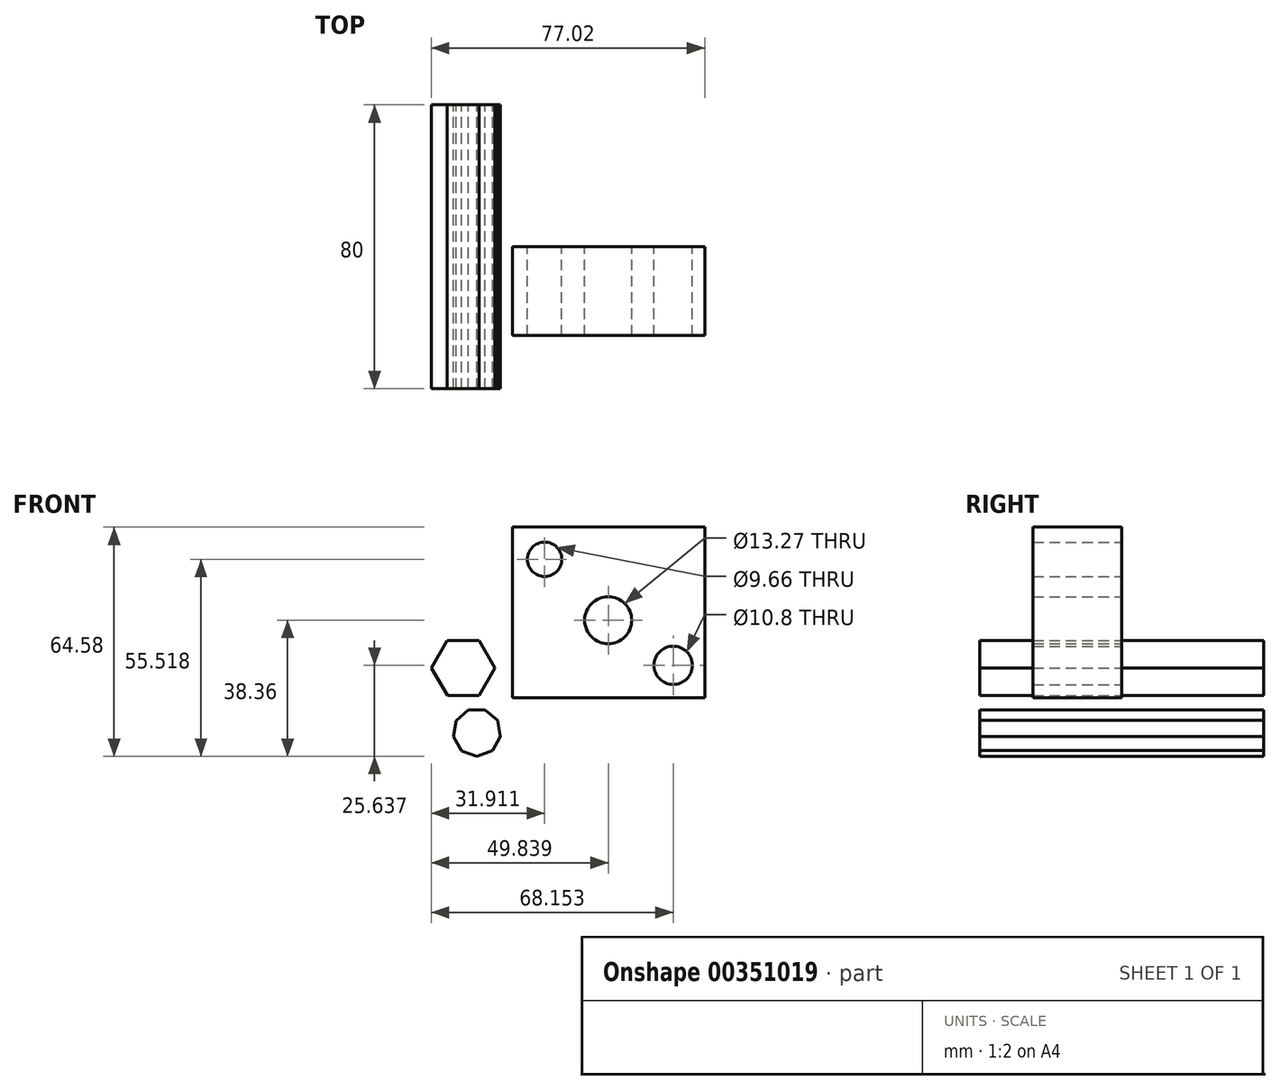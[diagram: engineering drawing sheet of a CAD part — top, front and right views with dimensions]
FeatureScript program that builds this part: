
annotation { "Feature Type Name" : "Feature", "Feature Type Description" : "" }
export const myFeature = defineFeature(function(context is Context, id is Id, definition is map)
    precondition{}
    {
        {
            var Q0;
            Q0=qCreatedBy(makeId("Front.planeOp"),FACE);
            var sketch = newSketch(context, id + "F0", { "sketchPlane" : qUnion([Q0])});
            skLineSegment(sketch, "E0.bottom", {"start": v(0, 0) * mm, "end": v(54.17, 0) * mm});
            skLineSegment(sketch, "E0.top", {"start": v(0, 48.1) * mm, "end": v(54.17, 48.1) * mm});
            skLineSegment(sketch, "E0.left", {"start": v(0, 0) * mm, "end": v(0, 48.1) * mm});
            skLineSegment(sketch, "E0.right", {"start": v(54.17, 0) * mm, "end": v(54.17, 48.1) * mm});
            skCircle(sketch, "E1", {"center": v(9.06, 39.04) * mm, "radius": 4.83 * mm});
            skCircle(sketch, "E2", {"center": v(26.99, 21.88) * mm, "radius": 6.63 * mm});
            skCircle(sketch, "E3", {"center": v(45.3, 9.16) * mm, "radius": 5.4 * mm});
            skSolve(sketch);
        }
        {
            var Q0;
            Q0=makeQuery(id+"F0.imprint","IMPRINT",FACE,{"disambiguationData":[TD([[makeQuery(id+"F0.imprint","IMPRINT",EDGE,{"derivedFrom":sQuery(id+"F0.wireOp",EDGE,"E0.bottom")}),1.0]])]});
            extrude(context, id + "F1", {"entities" : qUnion([Q0]), "depth" : 25 * mm});
        }
        {
            var Q0;
            Q0=qCreatedBy(makeId("Front.planeOp"),FACE);
            var sketch = newSketch(context, id + "F2", { "sketchPlane" : qUnion([Q0])});
            skCircle(sketch, "E4.cCircle", {"center": v(-10.02, -9.74) * mm, "radius": 6.34 * mm, "construction": true});
            skLineSegment(sketch, "E4.0", {"start": v(-9.97, -16.48) * mm, "end": v(-14.32, -14.94) * mm});
            skLineSegment(sketch, "E4.1", {"start": v(-14.32, -14.94) * mm, "end": v(-16.66, -10.96) * mm});
            skLineSegment(sketch, "E4.2", {"start": v(-16.66, -10.96) * mm, "end": v(-15.9, -6.4) * mm});
            skLineSegment(sketch, "E4.3", {"start": v(-15.9, -6.4) * mm, "end": v(-12.38, -3.41) * mm});
            skLineSegment(sketch, "E4.4", {"start": v(-12.38, -3.41) * mm, "end": v(-7.77, -3.38) * mm});
            skLineSegment(sketch, "E4.5", {"start": v(-7.77, -3.38) * mm, "end": v(-4.2, -6.31) * mm});
            skLineSegment(sketch, "E4.6", {"start": v(-4.2, -6.31) * mm, "end": v(-3.37, -10.85) * mm});
            skLineSegment(sketch, "E4.7", {"start": v(-3.37, -10.85) * mm, "end": v(-5.65, -14.87) * mm});
            skLineSegment(sketch, "E4.8", {"start": v(-5.65, -14.87) * mm, "end": v(-9.97, -16.48) * mm});
            skPoint(sketch, "E4.0.midPoint", {"position": v(-12.15, -15.71) * mm});
            skSolve(sketch);
        }
        {
            var Q0;
            Q0=makeQuery(id+"F2.imprint","IMPRINT",FACE,{"disambiguationData":[TD([[makeQuery(id+"F2.imprint","IMPRINT",EDGE,{"derivedFrom":sQuery(id+"F2.wireOp",EDGE,"E4.0")}),-1.0]])]});
            extrude(context, id + "F3", {"entities" : qUnion([Q0]), "endBound" : BoundingType.SYMMETRIC, "depth" : 80 * mm});
        }
        {
            var Q0;
            Q0=qCreatedBy(makeId("Front.planeOp"),FACE);
            var sketch = newSketch(context, id + "F4", { "sketchPlane" : qUnion([Q0])});
            skCircle(sketch, "E5.cCircle", {"center": v(-13.88, 8.39) * mm, "radius": 7.77 * mm, "construction": true});
            skLineSegment(sketch, "E5.0", {"start": v(-22.85, 8.35) * mm, "end": v(-18.4, 16.14) * mm});
            skLineSegment(sketch, "E5.1", {"start": v(-18.4, 16.14) * mm, "end": v(-9.43, 16.18) * mm});
            skLineSegment(sketch, "E5.2", {"start": v(-9.43, 16.18) * mm, "end": v(-4.9, 8.43) * mm});
            skLineSegment(sketch, "E5.3", {"start": v(-4.9, 8.43) * mm, "end": v(-9.36, 0.63) * mm});
            skLineSegment(sketch, "E5.4", {"start": v(-9.36, 0.63) * mm, "end": v(-18.33, 0.6) * mm});
            skLineSegment(sketch, "E5.5", {"start": v(-18.33, 0.6) * mm, "end": v(-22.85, 8.35) * mm});
            skPoint(sketch, "E5.0.midPoint", {"position": v(-20.63, 12.24) * mm});
            skSolve(sketch);
        }
        {
            var Q0;
            Q0=makeQuery(id+"F4.imprint","IMPRINT",FACE,{"disambiguationData":[TD([[makeQuery(id+"F4.imprint","IMPRINT",EDGE,{"derivedFrom":sQuery(id+"F4.wireOp",EDGE,"E5.0")}),-1.0]])]});
            extrude(context, id + "F5", {"entities" : qUnion([Q0]), "endBound" : BoundingType.SYMMETRIC, "depth" : 80 * mm});
        }
    });
